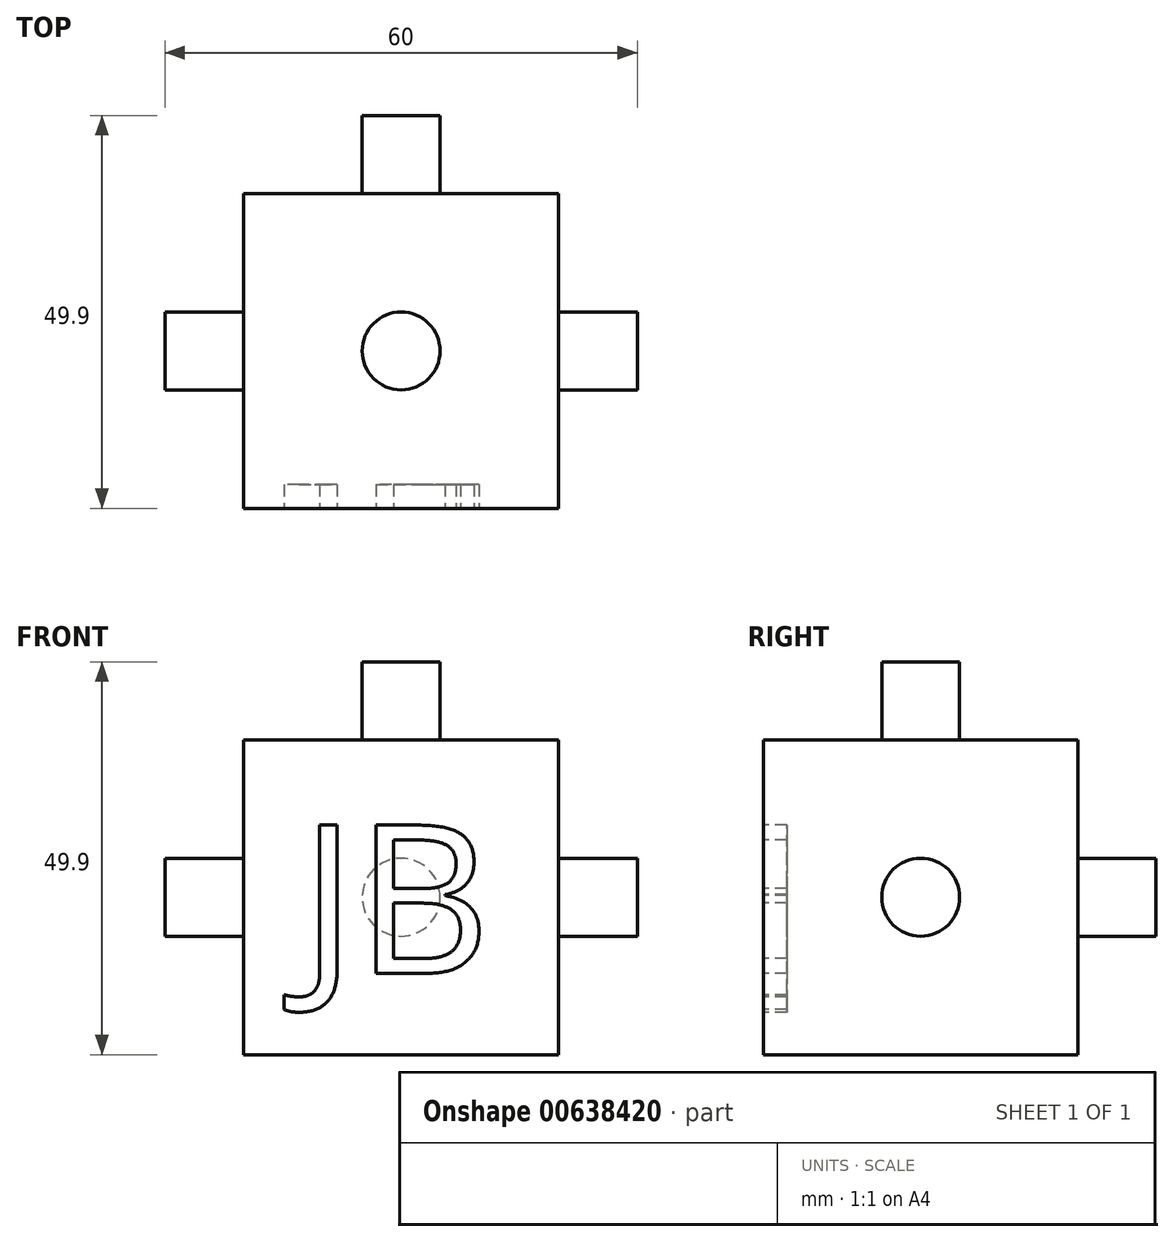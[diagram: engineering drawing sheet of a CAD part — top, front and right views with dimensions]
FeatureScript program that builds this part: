
annotation { "Feature Type Name" : "Feature", "Feature Type Description" : "" }
export const myFeature = defineFeature(function(context is Context, id is Id, definition is map)
    precondition{}
    {
        {
            var Q0;
            Q0=qCreatedBy(makeId("Front.planeOp"),FACE);
            var sketch = newSketch(context, id + "F0", { "sketchPlane" : qUnion([Q0])});
            skLineSegment(sketch, "E0", {"start": v(0, 0) * mm, "end": v(0, 40) * mm});
            skLineSegment(sketch, "E1", {"start": v(0, 40) * mm, "end": v(40, 40) * mm});
            skLineSegment(sketch, "E2", {"start": v(40, 40) * mm, "end": v(40, 0) * mm});
            skLineSegment(sketch, "E3", {"start": v(40, 0) * mm, "end": v(0, 0) * mm});
            skSolve(sketch);
        }
        {
            var Q0;
            Q0 = qSketchRegion(id + "F0", true);
            extrude(context, id + "F1", {"entities" : qUnion([Q0]), "depth" : 40 * mm, "offsetDistance" : 25 * mm});
        }
        {
            var Q0;
            Q0=makeQuery(id+"F1.opExtrude","CAP_FACE",FACE,{"disambiguationData":[OSD([sQuery(id+"F0.wireOp",EDGE,"E0"),sQuery(id+"F0.wireOp",EDGE,"E1"),sQuery(id+"F0.wireOp",EDGE,"E2"),sQuery(id+"F0.wireOp",EDGE,"E3")])],"isStart":false});
            var sketch = newSketch(context, id + "F2", { "sketchPlane" : qUnion([Q0])});
            skText(sketch, "E4", { "text": "JB", "fontName": "OpenSans-Regular.ttf"});
            const initialGuessF2  = {"E4": [0.00722, 0.01034, 1, 0, 0.01898]};
            skSetInitialGuess(sketch, initialGuessF2);
            skSolve(sketch);
        }
        {
            var Q0;
            Q0 = qSketchRegion(id + "F2", true);
            extrude(context, id + "F3", {"entities" : qUnion([Q0]), "operationType" : NewBodyOperationType.REMOVE, "oppositeDirection" : true, "depth" : 3 * mm, "offsetDistance" : 25 * mm});
        }
        {
            var Q0;
            Q0=makeQuery(id+"F1.opExtrude","SWEPT_FACE",FACE,{"disambiguationData":[OSD([sQuery(id+"F0.wireOp",EDGE,"E2")])]});
            var sketch = newSketch(context, id + "F4", { "sketchPlane" : qUnion([Q0])});
            skCircle(sketch, "E5", {"center": v(-20, 20) * mm, "radius": 4.95 * mm});
            skPoint(sketch, "E5.centerSnap0", {"position": v(-20, 40) * mm});
            skPoint(sketch, "E5.centerSnap1", {"position": v(-40, 20) * mm});
            skSolve(sketch);
        }
        {
            var Q0;
            Q0 = qSketchRegion(id + "F4", true);
            extrude(context, id + "F5", {"entities" : qUnion([Q0]), "operationType" : NewBodyOperationType.ADD, "depth" : 10 * mm, "offsetDistance" : 25 * mm});
        }
        {
            var Q0;
            Q0=makeQuery(id+"F1.opExtrude","SWEPT_FACE",FACE,{"disambiguationData":[OSD([sQuery(id+"F0.wireOp",EDGE,"E0")])]});
            var sketch = newSketch(context, id + "F6", { "sketchPlane" : qUnion([Q0])});
            skCircle(sketch, "E6", {"center": v(20, 20) * mm, "radius": 4.95 * mm});
            skPoint(sketch, "E6.centerSnap0", {"position": v(20, 40) * mm});
            skPoint(sketch, "E6.centerSnap1", {"position": v(0, 20) * mm});
            skSolve(sketch);
        }
        {
            var Q0;
            Q0 = qSketchRegion(id + "F6", true);
            extrude(context, id + "F7", {"entities" : qUnion([Q0]), "operationType" : NewBodyOperationType.ADD, "depth" : 10 * mm, "offsetDistance" : 25 * mm});
        }
        {
            var Q0;
            Q0=makeQuery(id+"F1.opExtrude","CAP_FACE",FACE,{"disambiguationData":[OSD([sQuery(id+"F0.wireOp",EDGE,"E0"),sQuery(id+"F0.wireOp",EDGE,"E1"),sQuery(id+"F0.wireOp",EDGE,"E2"),sQuery(id+"F0.wireOp",EDGE,"E3")])],"isStart":true});
            var sketch = newSketch(context, id + "F8", { "sketchPlane" : qUnion([Q0])});
            skCircle(sketch, "E7", {"center": v(-20, 20) * mm, "radius": 4.95 * mm});
            skPoint(sketch, "E7.centerSnap0", {"position": v(-20, 40) * mm});
            skPoint(sketch, "E7.centerSnap1", {"position": v(-40, 20) * mm});
            skSolve(sketch);
        }
        {
            var Q0;
            Q0 = qSketchRegion(id + "F8", true);
            extrude(context, id + "F9", {"entities" : qUnion([Q0]), "operationType" : NewBodyOperationType.ADD, "depth" : 9.9 * mm, "offsetDistance" : 25 * mm});
        }
        {
            var Q0;
            Q0=makeQuery(id+"F1.opExtrude","SWEPT_FACE",FACE,{"disambiguationData":[OSD([sQuery(id+"F0.wireOp",EDGE,"E1")])]});
            var sketch = newSketch(context, id + "F10", { "sketchPlane" : qUnion([Q0])});
            skCircle(sketch, "E8", {"center": v(20, -20) * mm, "radius": 4.95 * mm});
            skPoint(sketch, "E8.centerSnap0", {"position": v(20, 0) * mm});
            skPoint(sketch, "E8.centerSnap1", {"position": v(0, -20) * mm});
            skSolve(sketch);
        }
        {
            var Q0;
            Q0 = qSketchRegion(id + "F10", true);
            extrude(context, id + "F11", {"entities" : qUnion([Q0]), "operationType" : NewBodyOperationType.ADD, "depth" : 9.9 * mm, "offsetDistance" : 25 * mm});
        }
    });
